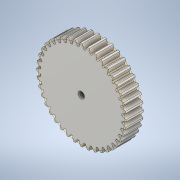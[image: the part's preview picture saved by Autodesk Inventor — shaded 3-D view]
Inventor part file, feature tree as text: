
AUTODESK INVENTOR PART (.ipt)
format: ipt  version: 2021 (Build 250183000, 183)  size: 337,920 bytes
history: native  units: mm (DEFAULTED — no unit token found)
features: sketch x4, plane x3, other x3, extrude x1, hole x1
ambient origin geometry x8: Origin, YZ Plane, XZ Plane, XY Plane, X Axis, Y Axis, Z Axis, Center Point
bodies: Solid1 (feature_tree)
feature tree (12):
  extrude  "Extrusion1"  Depth=8.0mm TaperAngle=0.0deg
  plane  "Work Plane2"
  plane  "Work Plane8"
  plane  "Work Plane9"
  other  "Spur Gear"
  sketch  "Sketch3"  dims[d16=25.351695mm]
  hole  "Hole1"  [1 undecoded]
  sketch  "Sketch1"  dims[d0=41.564361mm d1=8.0mm d2=0.0mm]
  sketch  "Sketch2"  dims[d3=40.0mm d4=10.0mm d5=0.0mm]
  other  "Srf1"
  sketch  "Sketch4"  dims[d17=0.0mm d34=0.785398mm d39=0.0mm d41=0.0mm d43=25.351695mm d46=25.351695mm d47=0.0mm d48=0.0mm d49=3.0mm d50=3.0mm d51=6.0mm d52=4.0mm d53=2.0mm d54=90.0deg d55=8.0mm d56=20.594885mm]
  other  "Pitch Diameter"
note: 1 required parameter value undecoded (feature->parameter linkage not recoverable at this tier; creation-order binding heuristic only, values carry confidence <= 0.55)
